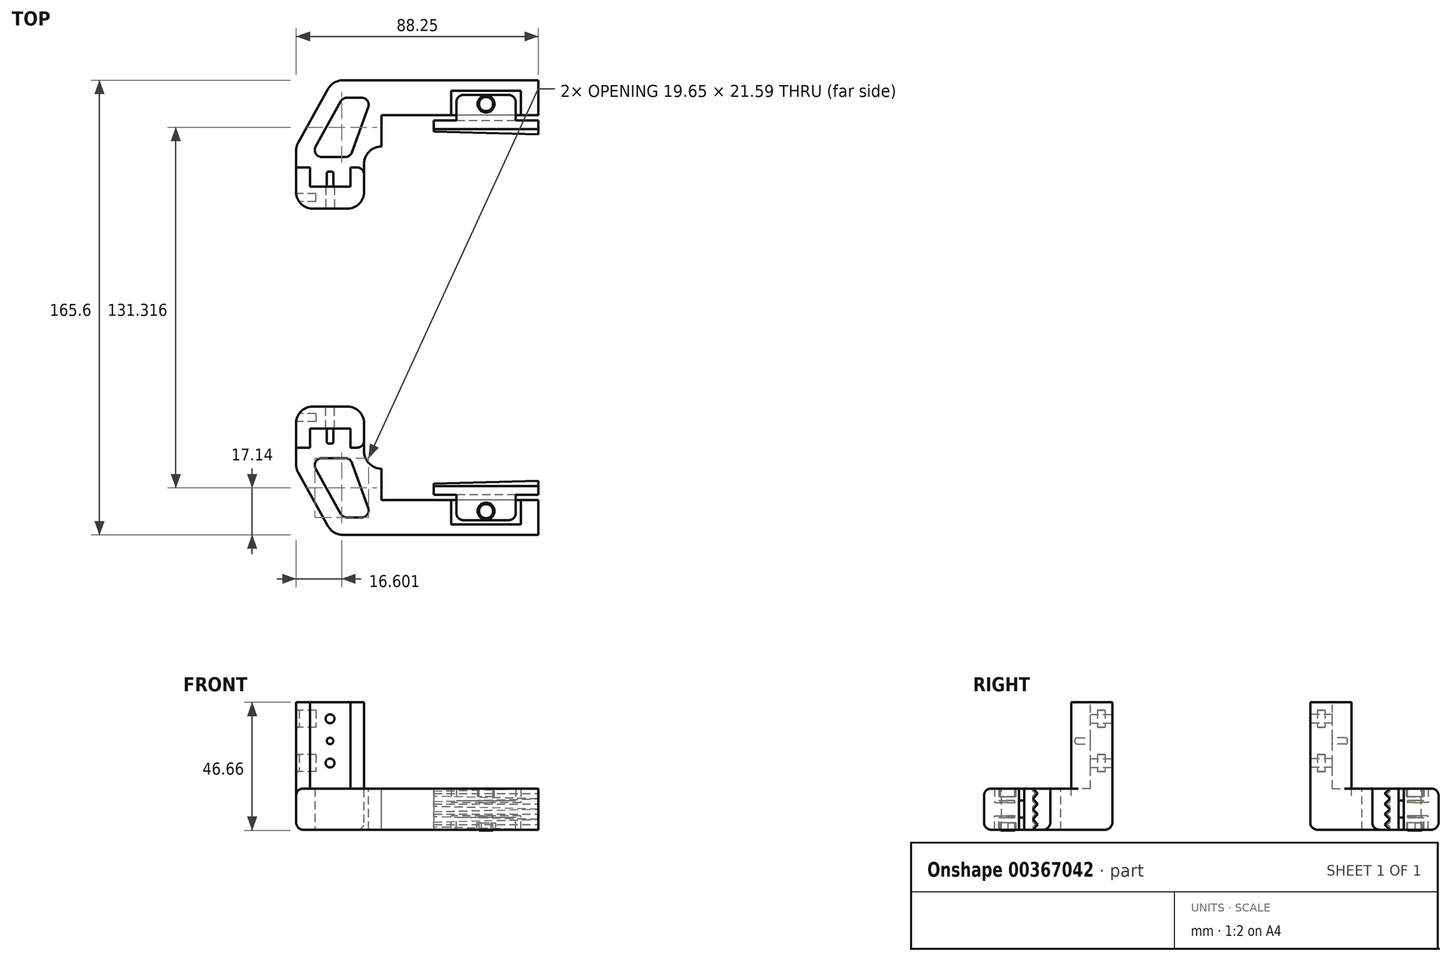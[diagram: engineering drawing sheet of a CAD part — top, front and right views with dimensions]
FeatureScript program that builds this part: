
annotation { "Feature Type Name" : "Feature", "Feature Type Description" : "" }
export const myFeature = defineFeature(function(context is Context, id is Id, definition is map)
    precondition{}
    {
        {
            assignVariable(context, id + "F0", {"name" : "squareNutWidth", "anyValue" : .215});
        }
        {
            var Q0;
            Q0=qCreatedBy(makeId("Front.planeOp"),FACE);
            var sketch = newSketch(context, id + "F1", { "sketchPlane" : qUnion([Q0])});
            skLineSegment(sketch, "E0.bottom", {"start": v(0, 0) * mm, "end": v(-14.75, 0) * mm});
            skLineSegment(sketch, "E0.top", {"start": v(0, 31.42) * mm, "end": v(-14.75, 31.42) * mm});
            skLineSegment(sketch, "E0.left", {"start": v(0, 0) * mm, "end": v(0, 31.42) * mm});
            skLineSegment(sketch, "E0.right", {"start": v(-14.75, 0) * mm, "end": v(-14.75, 31.42) * mm});
            skCircle(sketch, "E1", {"center": v(-7.38, 25.42) * mm, "radius": 1.63 * mm});
            skCircle(sketch, "E2", {"center": v(-7.38, 17.35) * mm, "radius": 1.5 * mm});
            skCircle(sketch, "E3", {"center": v(-7.38, 9.27) * mm, "radius": 1.63 * mm});
            skLineSegment(sketch, "E4", {"start": v(-7.38, 31.42) * mm, "end": v(-7.38, 0) * mm, "construction": true});
            skLineSegment(sketch, "E5", {"start": v(-9, 25.42) * mm, "end": v(-8.88, 17.35) * mm, "construction": true});
            skLineSegment(sketch, "E6", {"start": v(-8.88, 17.35) * mm, "end": v(-9, 9.27) * mm, "construction": true});
            skPoint(sketch, "E7", {"position": v(0, 15.71) * mm});
            skSolve(sketch);
        }
        {
            var Q0;
            Q0=makeQuery(id+"F1.imprint","IMPRINT",FACE,{"disambiguationData":[TD([[makeQuery(id+"F1.imprint","IMPRINT",EDGE,{"derivedFrom":sQuery(id+"F1.wireOp",EDGE,"E0.bottom")}),-1.0]])]});
            var Q1;
            Q1=makeQuery(id+"F1.imprint","IMPRINT",FACE,{"disambiguationData":[TD([[makeQuery(id+"F1.imprint","IMPRINT",EDGE,{"derivedFrom":sQuery(id+"F1.wireOp",EDGE,"E2")}),1.0]])]});
            extrude(context, id + "F2", {"entities" : qUnion([Q0, Q1]), "depth" : 8 * mm, "offsetDistance" : 25.4 * mm});
        }
        {
            var Q0;
            Q0=makeQuery(id+"F2.opExtrude","CAP_FACE",FACE,{"disambiguationData":[OSD([sQuery(id+"F1.wireOp",EDGE,"E0.bottom"),sQuery(id+"F1.wireOp",EDGE,"E0.top"),sQuery(id+"F1.wireOp",EDGE,"E0.left"),sQuery(id+"F1.wireOp",EDGE,"E0.right"),sQuery(id+"F1.wireOp",EDGE,"E1"),sQuery(id+"F1.wireOp",EDGE,"E3")])],"isStart":false});
            var sketch = newSketch(context, id + "F3", { "sketchPlane" : qUnion([Q0])});
            skLineSegment(sketch, "E8", {"start": v(-7.38, 25.42) * mm, "end": v(-7.38, 9.27) * mm, "construction": true});
            skCircle(sketch, "E9", {"center": v(-7.38, 17.35) * mm, "radius": 1.18 * mm});
            skSolve(sketch);
        }
        {
            var Q0;
            Q0=qSketchRegion(id+"F3",true);
            extrude(context, id + "F4", {"entities" : qUnion([Q0]), "operationType" : NewBodyOperationType.ADD, "depth" : 5.5 * mm});
        }
        {
            var Q0;
            Q0=makeQuery(id+"F4.opExtrude","CAP_EDGE",EDGE,{"disambiguationData":[OSD([sQuery(id+"F3.wireOp",EDGE,"E9")])],"isStart":false});
            fillet(context, id + "F5", {"entities" : qUnion([Q0]), "radius" : 0.64 * mm, "tangentPropagation" : true, "allowEdgeOverflow" : false});
        }
        {
            var Q0;
            Q0=makeQuery(id+"F2.opExtrude","SWEPT_FACE",FACE,{"disambiguationData":[OSD([sQuery(id+"F1.wireOp",EDGE,"E0.top")])]});
            var sketch = newSketch(context, id + "F6", { "sketchPlane" : qUnion([Q0])});
            skLineSegment(sketch, "E10.bottom", {"start": v(-14.75, 0) * mm, "end": v(-19.75, 0) * mm});
            skLineSegment(sketch, "E10.top", {"start": v(-14.75, -14.99) * mm, "end": v(-19.75, -14.99) * mm});
            skLineSegment(sketch, "E10.left", {"start": v(-14.75, 0) * mm, "end": v(-14.75, -14.99) * mm});
            skLineSegment(sketch, "E10.right", {"start": v(-19.75, 0) * mm, "end": v(-19.75, -14.99) * mm});
            skLineSegment(sketch, "E11.bottom", {"start": v(0, 0) * mm, "end": v(5, 0) * mm});
            skLineSegment(sketch, "E11.top", {"start": v(0, -14.98) * mm, "end": v(5, -14.98) * mm});
            skLineSegment(sketch, "E11.left", {"start": v(0, 0) * mm, "end": v(0, -14.98) * mm});
            skLineSegment(sketch, "E11.right", {"start": v(5, 0) * mm, "end": v(5, -14.98) * mm});
            skSolve(sketch);
        }
        {
            var Q0;
            Q0 = qSketchRegion(id + "F6", true);
            var Q1;
            Q1=makeQuery(id+"F2.opExtrude","SWEPT_FACE",FACE,{"disambiguationData":[OSD([sQuery(id+"F1.wireOp",EDGE,"E0.bottom")])]});
            extrude(context, id + "F7", {"entities" : qUnion([Q0]), "operationType" : NewBodyOperationType.ADD, "endBound" : BoundingType.UP_TO_SURFACE, "oppositeDirection" : true, "depth" : 25.4 * mm, "endBoundEntityFace" : qUnion([Q1]), "offsetDistance" : 25.4 * mm});
        }
        {
            var Q0;
            Q0=makeQuery(id+"F7.opExtrude","SWEPT_FACE",FACE,{"disambiguationData":[OSD([sQuery(id+"F6.wireOp",EDGE,"E10.right")])]});
            var sketch = newSketch(context, id + "F8", { "sketchPlane" : qUnion([Q0])});
            skLineSegment(sketch, "E12", {"start": v(4, 31.42) * mm, "end": v(4, 0) * mm, "construction": true});
            skLineSegment(sketch, "E13.bottom", {"start": v(2.57, 28.5) * mm, "end": v(5.43, 28.5) * mm});
            skLineSegment(sketch, "E13.top", {"start": v(2.57, 22.35) * mm, "end": v(5.43, 22.35) * mm});
            skLineSegment(sketch, "E13.left", {"start": v(2.57, 28.5) * mm, "end": v(2.57, 22.35) * mm});
            skLineSegment(sketch, "E13.right", {"start": v(5.43, 28.5) * mm, "end": v(5.43, 22.35) * mm});
            skLineSegment(sketch, "E14.bottom", {"start": v(2.57, 12.34) * mm, "end": v(5.43, 12.34) * mm});
            skLineSegment(sketch, "E14.top", {"start": v(2.57, 6.2) * mm, "end": v(5.43, 6.2) * mm});
            skLineSegment(sketch, "E14.left", {"start": v(2.57, 12.34) * mm, "end": v(2.57, 6.2) * mm});
            skLineSegment(sketch, "E14.right", {"start": v(5.43, 12.34) * mm, "end": v(5.43, 6.2) * mm});
            skPoint(sketch, "E15", {"position": v(2.57, 25.42) * mm});
            skPoint(sketch, "E16", {"position": v(2.57, 9.27) * mm});
            skPoint(sketch, "E17", {"position": v(4, 12.34) * mm});
            skPoint(sketch, "E18", {"position": v(4, 28.5) * mm});
            skLineSegment(sketch, "E19", {"start": v(0, 31.42) * mm, "end": v(8, 31.42) * mm, "construction": true});
            skSolve(sketch);
        }
        {
            var Q0;
            Q0=qSketchRegion(id+"F8",true);
            extrude(context, id + "F9", {"entities" : qUnion([Q0]), "operationType" : NewBodyOperationType.REMOVE, "oppositeDirection" : true, "depth" : 1.12 / 2 * (getVariable(context, 'squareNutWidth') + 0.56) * mm + 1.12 * 6 * mm, "offsetDistance" : 25.4 * mm});
        }
        {
            var Q0;
            Q0=makeQuery(id+"F2.opExtrude","SWEPT_FACE",FACE,{"disambiguationData":[OSD([sQuery(id+"F1.wireOp",EDGE,"E0.bottom")])]});
            var sketch = newSketch(context, id + "F10", { "sketchPlane" : qUnion([Q0])});
            skLineSegment(sketch, "E20", {"start": v(-6.34, 46.74) * mm, "end": v(68.5, 46.74) * mm});
            skLineSegment(sketch, "E21", {"start": v(68.5, 46.74) * mm, "end": v(68.5, 34.04) * mm});
            skLineSegment(sketch, "E22", {"start": v(68.5, 34.04) * mm, "end": v(11.35, 34.04) * mm});
            skLineSegment(sketch, "E23", {"start": v(-19.75, 14.99) * mm, "end": v(-19.75, 0) * mm});
            skLineSegment(sketch, "E24", {"start": v(-19.75, 0) * mm, "end": v(5, 0) * mm});
            skLineSegment(sketch, "E25", {"start": v(5, 0) * mm, "end": v(5, 14.98) * mm});
            skLineSegment(sketch, "E26", {"start": v(-19.75, 14.99) * mm, "end": v(-19.75, 22.6) * mm});
            skLineSegment(sketch, "E27", {"start": v(-19.75, 22.6) * mm, "end": v(-6.34, 46.74) * mm});
            skLineSegment(sketch, "E28", {"start": v(11.35, 34.04) * mm, "end": v(5, 22.6) * mm});
            skLineSegment(sketch, "E29", {"start": v(5, 22.6) * mm, "end": v(5, 14.98) * mm});
            skLineSegment(sketch, "E30", {"start": v(11.35, 34.04) * mm, "end": v(11.35, 22.6) * mm});
            skLineSegment(sketch, "E31", {"start": v(11.35, 22.6) * mm, "end": v(5, 22.6) * mm});
            skLineSegment(sketch, "E32", {"start": v(-14.75, 18.8) * mm, "end": v(-2.76, 40.39) * mm});
            skLineSegment(sketch, "E33", {"start": v(-2.76, 40.39) * mm, "end": v(7.76, 40.39) * mm});
            skLineSegment(sketch, "E34", {"start": v(0, 18.8) * mm, "end": v(-14.75, 18.8) * mm});
            skLineSegment(sketch, "E35", {"start": v(-14.75, 18.8) * mm, "end": v(-19.75, 18.8) * mm, "construction": true});
            skLineSegment(sketch, "E36", {"start": v(0, 18.8) * mm, "end": v(5, 18.8) * mm, "construction": true});
            skLineSegment(sketch, "E37", {"start": v(-6.34, 46.74) * mm, "end": v(11.35, 34.04) * mm, "construction": true});
            skPoint(sketch, "E38", {"position": v(2.5, 40.39) * mm});
            skLineSegment(sketch, "E39", {"start": v(0, 18.8) * mm, "end": v(7.76, 40.39) * mm});
            skSolve(sketch);
        }
        {
            var Q0;
            Q0 = qSketchRegion(id + "F10", true);
            extrude(context, id + "F11", {"entities" : qUnion([Q0]), "operationType" : NewBodyOperationType.ADD, "depth" : 15 * mm, "offsetDistance" : 25.4 * mm});
        }
        {
            var Q0;
            Q0=makeQuery(id+"F11.boolean.opBoolean","MERGE",EDGE,{"derivedFrom":[makeQuery(id+"F7.opExtrude","SWEPT_EDGE",EDGE,{"disambiguationData":[OSD([sQuery(id+"F6.wireOp",EDGE,"E10.bottom"),sQuery(id+"F6.wireOp",EDGE,"E10.right")])]}),makeQuery(id+"F11.opExtrude","SWEPT_EDGE",EDGE,{"disambiguationData":[OSD([sQuery(id+"F10.wireOp",EDGE,"E23"),sQuery(id+"F10.wireOp",EDGE,"E24")])]})]});
            var Q1;
            Q1=makeQuery(id+"F11.boolean.opBoolean","MERGE",EDGE,{"derivedFrom":[makeQuery(id+"F7.opExtrude","SWEPT_EDGE",EDGE,{"disambiguationData":[OSD([sQuery(id+"F6.wireOp",EDGE,"E11.bottom"),sQuery(id+"F6.wireOp",EDGE,"E11.right")])]}),makeQuery(id+"F11.opExtrude","SWEPT_EDGE",EDGE,{"disambiguationData":[OSD([sQuery(id+"F10.wireOp",EDGE,"E24"),sQuery(id+"F10.wireOp",EDGE,"E25")])]})]});
            var Q2;
            Q2=makeQuery(id+"F7.opExtrude","CAP_EDGE",EDGE,{"disambiguationData":[OSD([sQuery(id+"F6.wireOp",EDGE,"E10.top")])],"isStart":false});
            var Q3;
            Q3=makeQuery(id+"F7.opExtrude","CAP_EDGE",EDGE,{"disambiguationData":[OSD([sQuery(id+"F6.wireOp",EDGE,"E11.top")])],"isStart":false});
            var Q4;
            Q4=makeQuery(id+"F11.opExtrude","SWEPT_EDGE",EDGE,{"disambiguationData":[OSD([sQuery(id+"F10.wireOp",EDGE,"E26"),sQuery(id+"F10.wireOp",EDGE,"E27")])]});
            var Q5;
            Q5=makeQuery(id+"F11.opExtrude","SWEPT_EDGE",EDGE,{"disambiguationData":[OSD([sQuery(id+"F10.wireOp",EDGE,"E20"),sQuery(id+"F10.wireOp",EDGE,"E27")])]});
            fillet(context, id + "F12", {"entities" : qUnion([Q0, Q1, Q2, Q3, Q4, Q5]), "radius" : 6 * mm, "tangentPropagation" : true, "allowEdgeOverflow" : false});
        }
        {
            var Q0;
            Q0=makeQuery(id+"F11.opExtrude","SWEPT_EDGE",EDGE,{"disambiguationData":[OSD([sQuery(id+"F10.wireOp",EDGE,"E28"),sQuery(id+"F10.wireOp",EDGE,"E29"),sQuery(id+"F10.wireOp",EDGE,"E31")])]});
            fillet(context, id + "F13", {"entities" : qUnion([Q0]), "radius" : 6.35 * mm, "tangentPropagation" : true, "allowEdgeOverflow" : false});
        }
        {
            var Q0;
            Q0=makeQuery(id+"F11.opExtrude","SWEPT_EDGE",EDGE,{"disambiguationData":[OSD([sQuery(id+"F10.wireOp",EDGE,"E34"),sQuery(id+"F10.wireOp",EDGE,"E39")])]});
            var Q1;
            Q1=makeQuery(id+"F11.opExtrude","SWEPT_EDGE",EDGE,{"disambiguationData":[OSD([sQuery(id+"F10.wireOp",EDGE,"E32"),sQuery(id+"F10.wireOp",EDGE,"E34")])]});
            var Q2;
            Q2=makeQuery(id+"F11.opExtrude","SWEPT_EDGE",EDGE,{"disambiguationData":[OSD([sQuery(id+"F10.wireOp",EDGE,"E33"),sQuery(id+"F10.wireOp",EDGE,"E39")])]});
            var Q3;
            Q3=makeQuery(id+"F11.opExtrude","SWEPT_EDGE",EDGE,{"disambiguationData":[OSD([sQuery(id+"F10.wireOp",EDGE,"E32"),sQuery(id+"F10.wireOp",EDGE,"E33")])]});
            var Q4;
            Q4=makeQuery(id+"F11.opExtrude","CAP_EDGE",EDGE,{"disambiguationData":[OSD([sQuery(id+"F10.wireOp",EDGE,"E20")])],"isStart":true});
            var Q5;
            Q5=makeQuery(id+"F11.opExtrude","CAP_EDGE",EDGE,{"disambiguationData":[OSD([sQuery(id+"F10.wireOp",EDGE,"E20")])],"isStart":false});
            var Q6;
            Q6=makeQuery(id+"F7.opExtrude","SWEPT_EDGE",EDGE,{"disambiguationData":[OSD([sQuery(id+"F6.wireOp",EDGE,"E11.top"),sQuery(id+"F6.wireOp",EDGE,"E11.right")])]});
            fillet(context, id + "F14", {"entities" : qUnion([Q0, Q1, Q2, Q3, Q4, Q5, Q6]), "radius" : 2.54 * mm, "tangentPropagation" : true, "allowEdgeOverflow" : false});
        }
        {
            var Q0;
            Q0=makeQuery(id+"F11.opExtrude","SWEPT_FACE",FACE,{"disambiguationData":[OSD([sQuery(id+"F10.wireOp",EDGE,"E22")])]});
            var sketch = newSketch(context, id + "F15", { "sketchPlane" : qUnion([Q0])});
            skLineSegment(sketch, "E40.bottom", {"start": v(-62.15, 0) * mm, "end": v(-36.75, 0) * mm});
            skLineSegment(sketch, "E40.top", {"start": v(-62.15, -5.08) * mm, "end": v(-36.75, -5.08) * mm});
            skLineSegment(sketch, "E40.left", {"start": v(-62.15, 0) * mm, "end": v(-62.15, -5.08) * mm});
            skLineSegment(sketch, "E40.right", {"start": v(-36.75, 0) * mm, "end": v(-36.75, -5.08) * mm});
            skLineSegment(sketch, "E41.bottom", {"start": v(-62.15, -15) * mm, "end": v(-36.75, -15) * mm});
            skLineSegment(sketch, "E41.top", {"start": v(-62.15, -9.92) * mm, "end": v(-36.75, -9.92) * mm});
            skLineSegment(sketch, "E41.left", {"start": v(-62.15, -15) * mm, "end": v(-62.15, -9.92) * mm});
            skLineSegment(sketch, "E41.right", {"start": v(-36.75, -15) * mm, "end": v(-36.75, -9.92) * mm});
            skLineSegment(sketch, "E42", {"start": v(-62.15, -5.08) * mm, "end": v(-62.15, -9.92) * mm, "construction": true});
            skLineSegment(sketch, "E43", {"start": v(-36.75, -5.08) * mm, "end": v(-36.75, -9.92) * mm, "construction": true});
            skSolve(sketch);
        }
        {
            var Q0;
            Q0 = qSketchRegion(id + "F15", true);
            extrude(context, id + "F16", {"entities" : qUnion([Q0]), "operationType" : NewBodyOperationType.REMOVE, "oppositeDirection" : true, "depth" : 8.9 * mm, "offsetDistance" : 25.4 * mm});
        }
        {
            var Q0;
            Q0=makeQuery(id+"F11.opExtrude","SWEPT_FACE",FACE,{"disambiguationData":[OSD([sQuery(id+"F10.wireOp",EDGE,"E22")])]});
            cPlane(context, id + "F17", {"entities" : qUnion([Q0]), "cplaneType" : CPlaneType.OFFSET, "offset" : 1.9 * mm, "width" : 152.4 * mm, "height" : 152.4 * mm});
        }
        {
            var Q0;
            Q0=qCreatedBy(id+"F17.planeOp",FACE);
            var sketch = newSketch(context, id + "F18", { "sketchPlane" : qUnion([Q0])});
            skLineSegment(sketch, "E44.bottom", {"start": v(-68.5, 0) * mm, "end": v(-30.4, 0) * mm});
            skLineSegment(sketch, "E44.top", {"start": v(-68.5, -15) * mm, "end": v(-30.4, -15) * mm});
            skLineSegment(sketch, "E44.left", {"start": v(-68.5, 0) * mm, "end": v(-68.5, -15) * mm});
            skLineSegment(sketch, "E44.right", {"start": v(-30.4, 0) * mm, "end": v(-30.4, -15) * mm});
            skSolve(sketch);
        }
        {
            var Q0;
            Q0 = qSketchRegion(id + "F18", true);
            extrude(context, id + "F19", {"entities" : qUnion([Q0]), "depth" : 3.17 * mm, "offsetDistance" : 25.4 * mm});
        }
        {
            var Q0;
            Q0=makeQuery(id+"F19.opExtrude","SWEPT_FACE",FACE,{"disambiguationData":[OSD([sQuery(id+"F18.wireOp",EDGE,"E44.left")])]});
            var sketch = newSketch(context, id + "F20", { "sketchPlane" : qUnion([Q0])});
            skLineSegment(sketch, "E45", {"start": v(-28.96, 0) * mm, "end": v(-27.08, -1.88) * mm});
            skLineSegment(sketch, "E46", {"start": v(-27.08, -1.88) * mm, "end": v(-28.96, -3.75) * mm});
            skLineSegment(sketch, "E47", {"start": v(-28.96, -3.75) * mm, "end": v(-27.08, -5.63) * mm});
            skLineSegment(sketch, "E48", {"start": v(-27.08, -5.62) * mm, "end": v(-28.96, -7.5) * mm});
            skLineSegment(sketch, "E49", {"start": v(-28.96, -7.5) * mm, "end": v(-27.08, -9.38) * mm});
            skLineSegment(sketch, "E50", {"start": v(-27.08, -9.38) * mm, "end": v(-28.96, -11.25) * mm});
            skLineSegment(sketch, "E51", {"start": v(-28.96, -11.25) * mm, "end": v(-27.08, -13.13) * mm});
            skLineSegment(sketch, "E52", {"start": v(-27.08, -13.12) * mm, "end": v(-28.96, -15) * mm});
            skLineSegment(sketch, "E53", {"start": v(-28.96, 0) * mm, "end": v(-32.13, 0) * mm});
            skLineSegment(sketch, "E54", {"start": v(-32.13, 0) * mm, "end": v(-32.13, -15) * mm});
            skLineSegment(sketch, "E55", {"start": v(-32.13, -15) * mm, "end": v(-28.96, -15) * mm});
            skSolve(sketch);
        }
        {
            var Q0;
            Q0 = qSketchRegion(id + "F20", true);
            var Q1;
            Q1=makeQuery(id+"F19.opExtrude","SWEPT_FACE",FACE,{"disambiguationData":[OSD([sQuery(id+"F18.wireOp",EDGE,"E44.right")])]});
            extrude(context, id + "F21", {"entities" : qUnion([Q0]), "operationType" : NewBodyOperationType.ADD, "endBound" : BoundingType.UP_TO_SURFACE, "oppositeDirection" : true, "depth" : 25.4 * mm, "endBoundEntityFace" : qUnion([Q1]), "offsetDistance" : 25.4 * mm, "hasDraft" : true, "draftAngle" : 1 * degree, "draftPullDirection" : true});
        }
        {
            var Q0;
            Q0=makeQuery(id+"F19.opExtrude","CAP_FACE",FACE,{"disambiguationData":[OSD([sQuery(id+"F18.wireOp",EDGE,"E44.bottom"),sQuery(id+"F18.wireOp",EDGE,"E44.top"),sQuery(id+"F18.wireOp",EDGE,"E44.left"),sQuery(id+"F18.wireOp",EDGE,"E44.right")])],"isStart":true});
            var sketch = newSketch(context, id + "F22", { "sketchPlane" : qUnion([Q0])});
            skLineSegment(sketch, "E56.bottom", {"start": v(38.66, 0) * mm, "end": v(60.25, 0) * mm});
            skLineSegment(sketch, "E56.top", {"start": v(38.66, -4.36) * mm, "end": v(60.25, -4.36) * mm});
            skLineSegment(sketch, "E56.left", {"start": v(38.66, 0) * mm, "end": v(38.66, -4.36) * mm});
            skLineSegment(sketch, "E56.right", {"start": v(60.25, 0) * mm, "end": v(60.25, -4.36) * mm});
            skLineSegment(sketch, "E57.bottom", {"start": v(60.25, -15) * mm, "end": v(38.66, -15) * mm});
            skLineSegment(sketch, "E57.top", {"start": v(60.25, -10.64) * mm, "end": v(38.66, -10.64) * mm});
            skLineSegment(sketch, "E57.left", {"start": v(60.25, -15) * mm, "end": v(60.25, -10.64) * mm});
            skLineSegment(sketch, "E57.right", {"start": v(38.66, -15) * mm, "end": v(38.66, -10.64) * mm});
            skPoint(sketch, "E58", {"position": v(49.45, 0) * mm});
            skPoint(sketch, "E59", {"position": v(49.45, -4.36) * mm});
            skSolve(sketch);
        }
        {
            var Q0;
            Q0 = qSketchRegion(id + "F22", true);
            extrude(context, id + "F23", {"entities" : qUnion([Q0]), "operationType" : NewBodyOperationType.ADD, "depth" : 9.27 * mm, "offsetDistance" : 25.4 * mm});
        }
        {
            var Q0;
            Q0=makeQuery(id+"F23.boolean.opBoolean","MERGE",FACE,{"derivedFrom":[makeQuery(id+"F19.opExtrude","SWEPT_FACE",FACE,{"disambiguationData":[OSD([sQuery(id+"F18.wireOp",EDGE,"E44.bottom")])]}),makeQuery(id+"F23.opExtrude","SWEPT_FACE",FACE,{"disambiguationData":[OSD([sQuery(id+"F22.wireOp",EDGE,"E56.bottom")])]})]});
            var sketch = newSketch(context, id + "F24", { "sketchPlane" : qUnion([Q0])});
            skCircle(sketch, "E60", {"center": v(49.45, -38.1) * mm, "radius": 1.66 * mm});
            skSolve(sketch);
        }
        {
            var Q0;
            Q0 = qSketchRegion(id + "F24", true);
            extrude(context, id + "F25", {"entities" : qUnion([Q0]), "operationType" : NewBodyOperationType.REMOVE, "endBound" : BoundingType.THROUGH_ALL, "oppositeDirection" : true, "depth" : 25.4 * mm, "offsetDistance" : 25.4 * mm});
        }
        {
            var Q0;
            Q0=makeQuery(id+"F23.boolean.opBoolean","MERGE",FACE,{"derivedFrom":[makeQuery(id+"F19.opExtrude","SWEPT_FACE",FACE,{"disambiguationData":[OSD([sQuery(id+"F18.wireOp",EDGE,"E44.bottom")])]}),makeQuery(id+"F23.opExtrude","SWEPT_FACE",FACE,{"disambiguationData":[OSD([sQuery(id+"F22.wireOp",EDGE,"E56.bottom")])]})]});
            var sketch = newSketch(context, id + "F26", { "sketchPlane" : qUnion([Q0])});
            skCircle(sketch, "E61", {"center": v(49.45, -38.1) * mm, "radius": 3.07 * mm});
            skSolve(sketch);
        }
        {
            var Q0;
            Q0 = qSketchRegion(id + "F26", true);
            extrude(context, id + "F27", {"entities" : qUnion([Q0]), "operationType" : NewBodyOperationType.REMOVE, "oppositeDirection" : true, "depth" : 3 * mm, "offsetDistance" : 25.4 * mm});
        }
        {
            var Q0;
            Q0=makeQuery(id+"F23.boolean.opBoolean","MERGE",FACE,{"derivedFrom":[makeQuery(id+"F19.opExtrude","SWEPT_FACE",FACE,{"disambiguationData":[OSD([sQuery(id+"F18.wireOp",EDGE,"E44.top")])]}),makeQuery(id+"F23.opExtrude","SWEPT_FACE",FACE,{"disambiguationData":[OSD([sQuery(id+"F22.wireOp",EDGE,"E57.bottom")])]})]});
            var sketch = newSketch(context, id + "F28", { "sketchPlane" : qUnion([Q0])});
            skCircle(sketch, "E62.cCircle", {"center": v(49.45, 38.1) * mm, "radius": 3.01 * mm, "construction": true});
            skLineSegment(sketch, "E62.0", {"start": v(47.7, 41.11) * mm, "end": v(51.2, 41.11) * mm});
            skLineSegment(sketch, "E62.1", {"start": v(51.2, 41.11) * mm, "end": v(52.93, 38.1) * mm});
            skLineSegment(sketch, "E62.2", {"start": v(52.93, 38.1) * mm, "end": v(51.2, 35.08) * mm});
            skLineSegment(sketch, "E62.3", {"start": v(51.2, 35.08) * mm, "end": v(47.7, 35.08) * mm});
            skLineSegment(sketch, "E62.4", {"start": v(47.7, 35.08) * mm, "end": v(45.97, 38.1) * mm});
            skLineSegment(sketch, "E62.5", {"start": v(45.97, 38.1) * mm, "end": v(47.7, 41.11) * mm});
            skPoint(sketch, "E62.0.midPoint", {"position": v(49.45, 41.11) * mm});
            skSolve(sketch);
        }
        {
            var Q0;
            Q0 = qSketchRegion(id + "F28", true);
            extrude(context, id + "F29", {"entities" : qUnion([Q0]), "operationType" : NewBodyOperationType.REMOVE, "oppositeDirection" : true, "depth" : 2.5 * mm, "offsetDistance" : 25.4 * mm});
        }
        {
            var Q0;
            Q0=makeQuery(id+"F23.opExtrude","CAP_EDGE",EDGE,{"disambiguationData":[OSD([sQuery(id+"F22.wireOp",EDGE,"E56.left")])],"isStart":false});
            var Q1;
            Q1=makeQuery(id+"F23.opExtrude","CAP_EDGE",EDGE,{"disambiguationData":[OSD([sQuery(id+"F22.wireOp",EDGE,"E56.right")])],"isStart":false});
            var Q2;
            Q2=makeQuery(id+"F23.opExtrude","CAP_EDGE",EDGE,{"disambiguationData":[OSD([sQuery(id+"F22.wireOp",EDGE,"E57.left")])],"isStart":false});
            var Q3;
            Q3=makeQuery(id+"F23.opExtrude","CAP_EDGE",EDGE,{"disambiguationData":[OSD([sQuery(id+"F22.wireOp",EDGE,"E57.right")])],"isStart":false});
            fillet(context, id + "F30", {"entities" : qUnion([Q0, Q1, Q2, Q3]), "radius" : 2.54 * mm, "tangentPropagation" : true, "allowEdgeOverflow" : false});
        }
        {
            var Q0;
            Q0=makeQuery(id+"F23.boolean.opBoolean","MERGE",FACE,{"derivedFrom":[makeQuery(id+"F19.opExtrude","SWEPT_FACE",FACE,{"disambiguationData":[OSD([sQuery(id+"F18.wireOp",EDGE,"E44.bottom")])]}),makeQuery(id+"F23.opExtrude","SWEPT_FACE",FACE,{"disambiguationData":[OSD([sQuery(id+"F22.wireOp",EDGE,"E56.bottom")])]})]});
            var sketch = newSketch(context, id + "F31", { "sketchPlane" : qUnion([Q0])});
            skCircle(sketch, "E63", {"center": v(49.45, -38.1) * mm, "radius": 2.58 * mm});
            skSolve(sketch);
        }
        {
            var Q0;
            Q0 = qSketchRegion(id + "F31", true);
            extrude(context, id + "F32", {"entities" : qUnion([Q0]), "operationType" : NewBodyOperationType.ADD, "oppositeDirection" : true, "depth" : 15.24 * mm, "offsetDistance" : 25.4 * mm});
        }
        {
            var Q0;
            Q0=qCreatedBy(makeId("Front.planeOp"),FACE);
            cPlane(context, id + "F33", {"entities" : qUnion([Q0]), "cplaneType" : CPlaneType.OFFSET, "offset" : 36.07 * mm, "oppositeDirection" : true, "width" : 152.4 * mm, "height" : 152.4 * mm});
        }
        {
            var Q0;
            Q0=makeQuery(id+"F2.opExtrude","SWEPT_BODY",BODY,{"disambiguationData":[OSD([sQuery(id+"F1.wireOp",EDGE,"E0.bottom"),sQuery(id+"F1.wireOp",EDGE,"E0.top"),sQuery(id+"F1.wireOp",EDGE,"E0.left"),sQuery(id+"F1.wireOp",EDGE,"E0.right"),sQuery(id+"F1.wireOp",EDGE,"E1"),sQuery(id+"F1.wireOp",EDGE,"E3")])]});
            var Q1;
            Q1=makeQuery(id+"F19.opExtrude","SWEPT_BODY",BODY,{"disambiguationData":[OSD([sQuery(id+"F18.wireOp",EDGE,"E44.bottom"),sQuery(id+"F18.wireOp",EDGE,"E44.top"),sQuery(id+"F18.wireOp",EDGE,"E44.left"),sQuery(id+"F18.wireOp",EDGE,"E44.right")])]});
            var Q2;
            Q2=qCreatedBy(id+"F33.planeOp",FACE);
            mirror(context, id + "F34", {"entities" : qUnion([Q0, Q1]), "mirrorPlane" : qUnion([Q2])});
        }
    });
